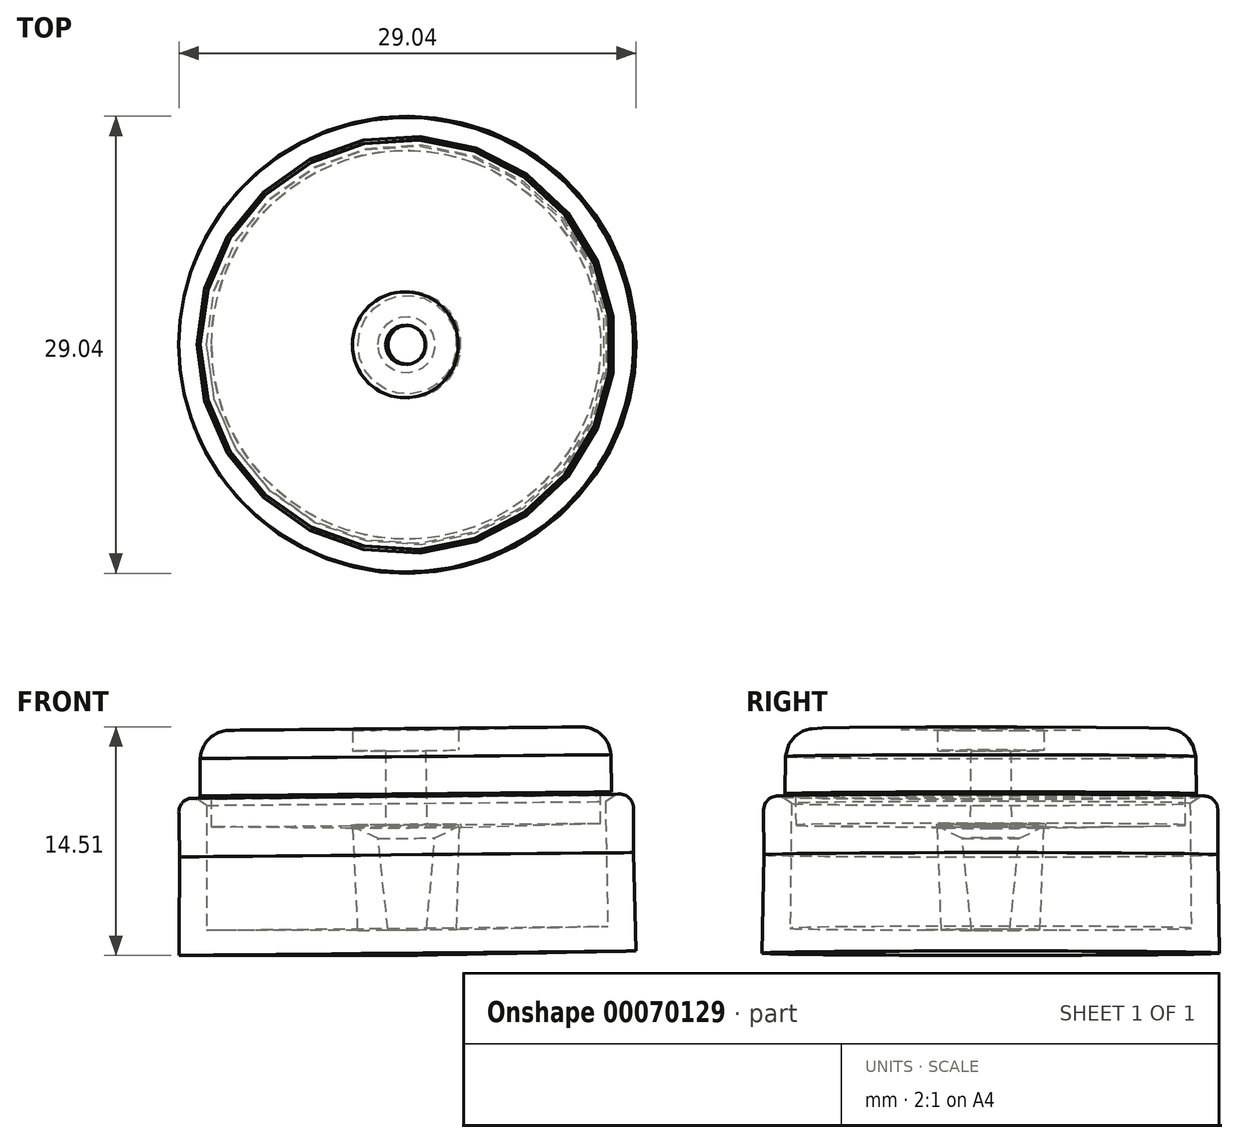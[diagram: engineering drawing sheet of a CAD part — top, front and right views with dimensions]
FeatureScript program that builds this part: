
annotation { "Feature Type Name" : "Feature", "Feature Type Description" : "" }
export const myFeature = defineFeature(function(context is Context, id is Id, definition is map)
    precondition{}
    {
        {
            var Q0;
            Q0=qCreatedBy(makeId("Front.planeOp"),FACE);
            var sketch = newSketch(context, id + "F0", { "sketchPlane" : qUnion([Q0])});
            skLineSegment(sketch, "E0", {"start": v(-14.52, 9.1) * mm, "end": v(-14.47, 6.25) * mm});
            skLineSegment(sketch, "E1", {"start": v(-14.47, 6.25) * mm, "end": v(-14.52, 0) * mm});
            skLineSegment(sketch, "E2", {"start": v(0, 0) * mm, "end": v(-14.52, 0) * mm});
            skLineSegment(sketch, "E3", {"start": v(-3.15, 1.6) * mm, "end": v(-12.75, 1.6) * mm});
            skLineSegment(sketch, "E4", {"start": v(-0.02, 1.6) * mm, "end": v(-1.24, 1.61) * mm});
            skLineSegment(sketch, "E5", {"start": v(0, 0) * mm, "end": v(-0.02, 1.6) * mm});
            skArc(sketch, "E6", {"start": v(-13.36, 9.93) * mm, "mid": v(-14.16, 9.82) * mm, "end": v(-14.52, 9.1) * mm});
            skLineSegment(sketch, "E7", {"start": v(-3.46, 8.16) * mm, "end": v(-1.87, 7.42) * mm});
            skLineSegment(sketch, "E8", {"start": v(-1.87, 7.42) * mm, "end": v(-1.24, 1.61) * mm});
            skLineSegment(sketch, "E9", {"start": v(-3.46, 8.16) * mm, "end": v(-3.15, 1.6) * mm});
            skLineSegment(sketch, "E10", {"start": v(-13.36, 9.93) * mm, "end": v(-12.75, 9.53) * mm});
            skLineSegment(sketch, "E11", {"start": v(-12.75, 9.53) * mm, "end": v(-12.75, 1.6) * mm});
            skSolve(sketch);
        }
        {
            var Q0;
            Q0=qCreatedBy(makeId("Front.planeOp"),FACE);
            var sketch = newSketch(context, id + "F1", { "sketchPlane" : qUnion([Q0])});
            skLineSegment(sketch, "E12", {"start": v(-3.54, 8.07) * mm, "end": v(-12.43, 8.16) * mm});
            skLineSegment(sketch, "E13", {"start": v(-3.54, 8.3) * mm, "end": v(-3.54, 8.07) * mm});
            skLineSegment(sketch, "E14", {"start": v(-13.16, 12.5) * mm, "end": v(-13.16, 10.13) * mm});
            skArc(sketch, "E15", {"start": v(-11.27, 14.3) * mm, "mid": v(-12.57, 13.77) * mm, "end": v(-13.16, 12.5) * mm});
            skLineSegment(sketch, "E16", {"start": v(-11.27, 14.3) * mm, "end": v(-3.5, 14.28) * mm});
            skLineSegment(sketch, "E17", {"start": v(-3.5, 14.28) * mm, "end": v(-3.5, 12.97) * mm});
            skLineSegment(sketch, "E18", {"start": v(-12.45, 10.14) * mm, "end": v(-13.16, 10.13) * mm});
            skLineSegment(sketch, "E19", {"start": v(-3.54, 8.3) * mm, "end": v(-1.39, 8.3) * mm});
            skLineSegment(sketch, "E20", {"start": v(-1.39, 8.3) * mm, "end": v(-1.39, 12.97) * mm});
            skLineSegment(sketch, "E21", {"start": v(-3.5, 12.97) * mm, "end": v(-1.39, 12.97) * mm});
            skLineSegment(sketch, "E22", {"start": v(-12.43, 8.16) * mm, "end": v(-12.45, 10.14) * mm});
            skSolve(sketch);
        }
        {
            var Q0;
            Q0=qSketchRegion(id+"F0",true);
            var Q1;
            Q1=sQuery(id+"F0.wireOp",EDGE,"E5");
            revolve(context, id + "F2", {"entities" : qUnion([Q0]), "axis" : qUnion([Q1]), "revolveType" : RevolveType.FULL});
        }
        {
            var Q0;
            Q0=qSketchRegion(id+"F1",true);
            var Q1;
            Q1=sQuery(id+"F0.wireOp",EDGE,"E5");
            revolve(context, id + "F3", {"entities" : qUnion([Q0]), "axis" : qUnion([Q1]), "revolveType" : RevolveType.FULL});
        }
    });
